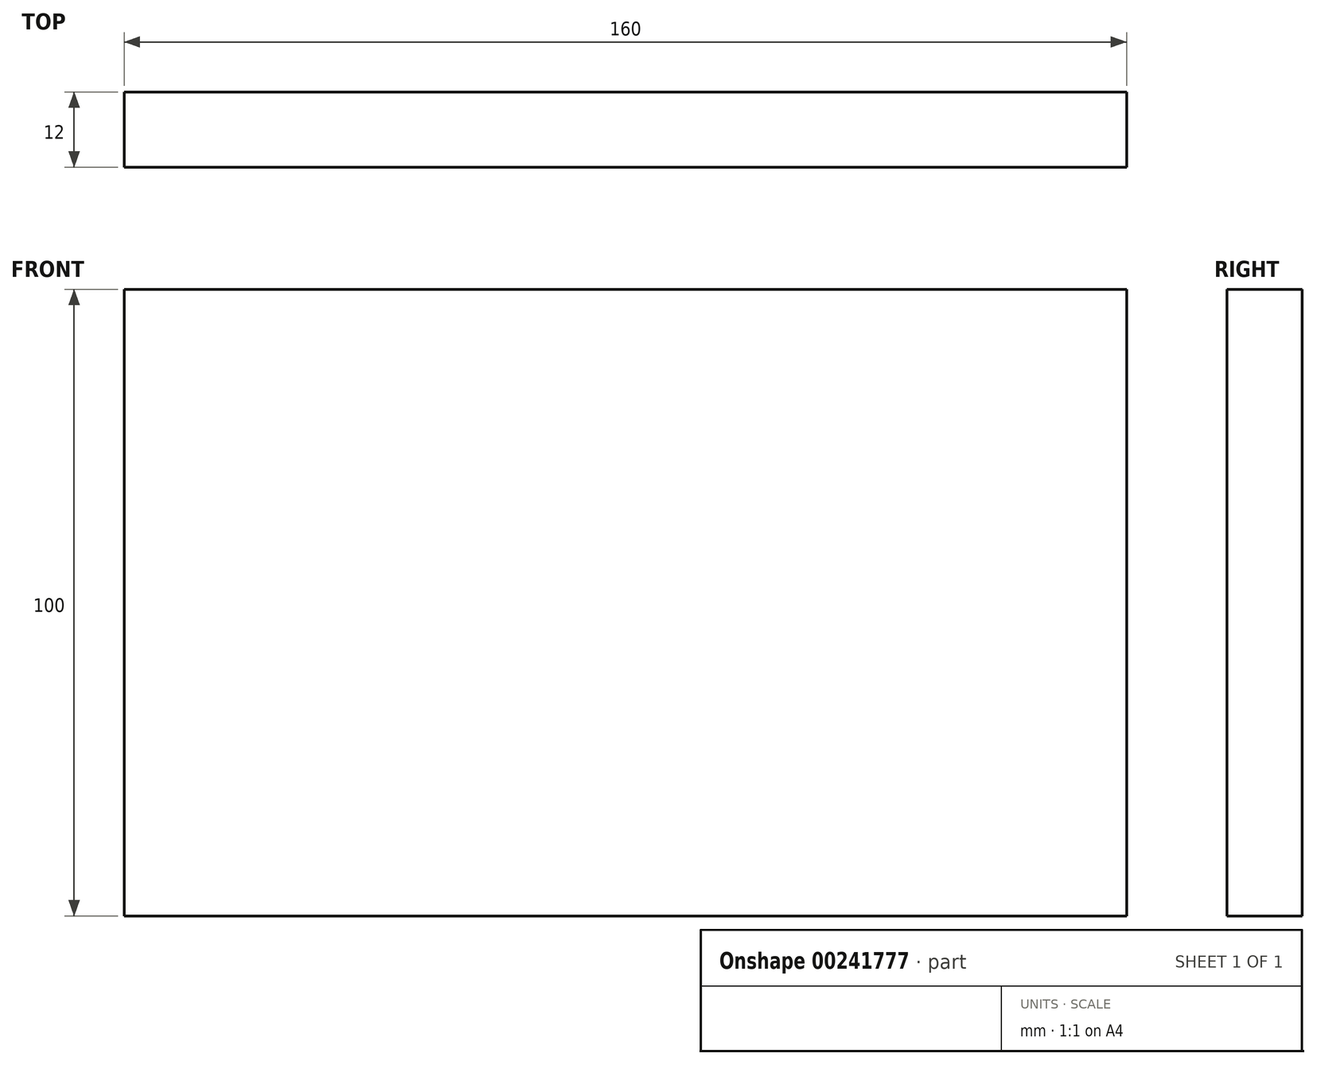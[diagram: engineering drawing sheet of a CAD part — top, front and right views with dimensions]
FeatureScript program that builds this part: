
annotation { "Feature Type Name" : "Feature", "Feature Type Description" : "" }
export const myFeature = defineFeature(function(context is Context, id is Id, definition is map)
    precondition{}
    {
        {
            var Q0;
            Q0=qCreatedBy(makeId("Front.planeOp"),FACE);
            var sketch = newSketch(context, id + "F0", { "sketchPlane" : qUnion([Q0])});
            skLineSegment(sketch, "E0.bottom", {"start": v(0, 0) * mm, "end": v(160, 0) * mm});
            skLineSegment(sketch, "E0.top", {"start": v(0, 100) * mm, "end": v(160, 100) * mm});
            skLineSegment(sketch, "E0.left", {"start": v(0, 0) * mm, "end": v(0, 100) * mm});
            skLineSegment(sketch, "E0.right", {"start": v(160, 0) * mm, "end": v(160, 100) * mm});
            skSolve(sketch);
        }
        {
            var Q0;
            Q0=qSketchRegion(id+"F0",true);
            extrude(context, id + "F1", {"entities" : qUnion([Q0]), "depth" : 12 * mm});
        }
    });
